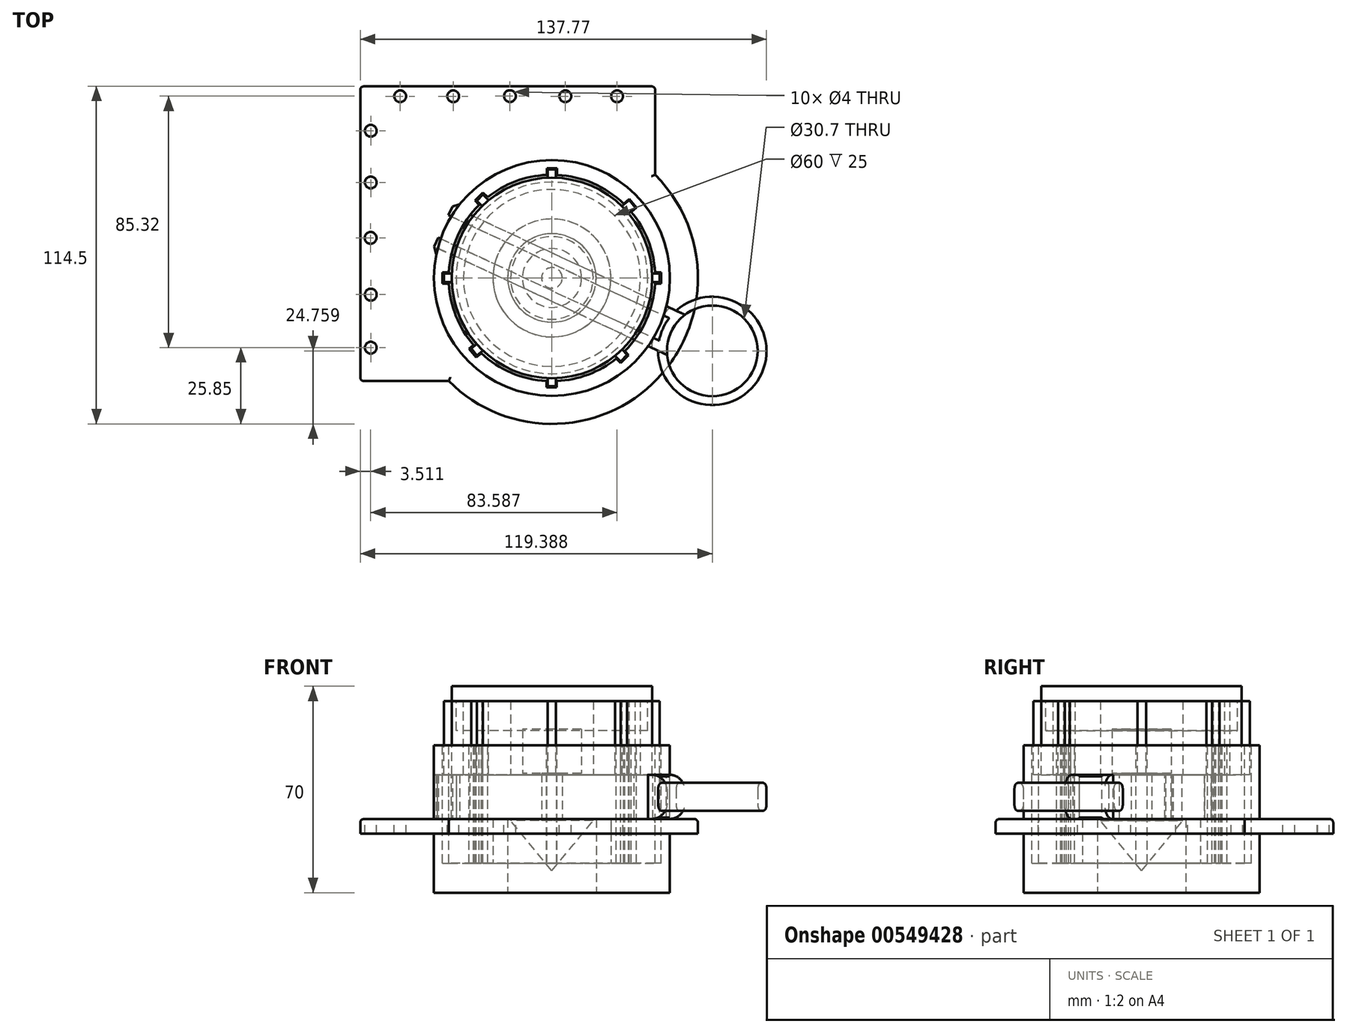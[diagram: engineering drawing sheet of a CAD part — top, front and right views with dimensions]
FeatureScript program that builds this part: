
annotation { "Feature Type Name" : "Feature", "Feature Type Description" : "" }
export const myFeature = defineFeature(function(context is Context, id is Id, definition is map)
    precondition{}
    {
        {
            var Q0;
            Q0=qCreatedBy(makeId("Top.planeOp"),FACE);
            var sketch = newSketch(context, id + "F0", { "sketchPlane" : qUnion([Q0])});
            skCircle(sketch, "E0", {"center": v(0, 0) * mm, "radius": 35 * mm});
            skCircle(sketch, "E1", {"center": v(0, 0) * mm, "radius": 40 * mm});
            skLineSegment(sketch, "E2.bottom", {"start": v(-1.72, 37.22) * mm, "end": v(1.75, 37.22) * mm});
            skLineSegment(sketch, "E2.top", {"start": v(-1.72, 33.39) * mm, "end": v(1.75, 33.39) * mm});
            skLineSegment(sketch, "E2.left", {"start": v(-1.72, 37.22) * mm, "end": v(-1.72, 33.39) * mm});
            skLineSegment(sketch, "E2.right", {"start": v(1.75, 37.22) * mm, "end": v(1.75, 33.39) * mm});
            skLineSegment(sketch, "E3.bottom", {"start": v(-23.4, 28.93) * mm, "end": v(-20.95, 26.48) * mm});
            skLineSegment(sketch, "E3.top", {"start": v(-26.11, 26.22) * mm, "end": v(-23.66, 23.77) * mm});
            skLineSegment(sketch, "E3.left", {"start": v(-23.4, 28.93) * mm, "end": v(-26.11, 26.22) * mm});
            skLineSegment(sketch, "E3.right", {"start": v(-20.95, 26.48) * mm, "end": v(-23.66, 23.77) * mm});
            skLineSegment(sketch, "E4.bottom", {"start": v(-37.15, 1.95) * mm, "end": v(-33.68, 1.95) * mm});
            skLineSegment(sketch, "E4.top", {"start": v(-37.15, -1.88) * mm, "end": v(-33.68, -1.88) * mm});
            skLineSegment(sketch, "E4.left", {"start": v(-37.15, 1.95) * mm, "end": v(-37.15, -1.88) * mm});
            skLineSegment(sketch, "E4.right", {"start": v(-33.68, 1.95) * mm, "end": v(-33.68, -1.88) * mm});
            skLineSegment(sketch, "E5.bottom", {"start": v(1.65, -37.15) * mm, "end": v(-1.82, -37.15) * mm});
            skLineSegment(sketch, "E5.top", {"start": v(1.65, -33.31) * mm, "end": v(-1.82, -33.31) * mm});
            skLineSegment(sketch, "E5.left", {"start": v(1.65, -37.15) * mm, "end": v(1.65, -33.31) * mm});
            skLineSegment(sketch, "E5.right", {"start": v(-1.82, -37.15) * mm, "end": v(-1.82, -33.31) * mm});
            skLineSegment(sketch, "E6.bottom", {"start": v(23.33, -28.86) * mm, "end": v(20.88, -26.41) * mm});
            skLineSegment(sketch, "E6.top", {"start": v(26.04, -26.15) * mm, "end": v(23.6, -23.7) * mm});
            skLineSegment(sketch, "E6.left", {"start": v(23.33, -28.86) * mm, "end": v(26.04, -26.15) * mm});
            skLineSegment(sketch, "E6.right", {"start": v(20.88, -26.41) * mm, "end": v(23.6, -23.7) * mm});
            skLineSegment(sketch, "E7.bottom", {"start": v(37.08, -1.88) * mm, "end": v(33.61, -1.88) * mm});
            skLineSegment(sketch, "E7.top", {"start": v(37.08, 1.95) * mm, "end": v(33.61, 1.95) * mm});
            skLineSegment(sketch, "E7.left", {"start": v(37.08, -1.88) * mm, "end": v(37.08, 1.95) * mm});
            skLineSegment(sketch, "E7.right", {"start": v(33.61, -1.88) * mm, "end": v(33.61, 1.95) * mm});
            skLineSegment(sketch, "E8.bottom", {"start": v(-28.15, -24) * mm, "end": v(-25.5, -21.78) * mm});
            skLineSegment(sketch, "E8.top", {"start": v(-25.68, -26.94) * mm, "end": v(-23.03, -24.71) * mm});
            skLineSegment(sketch, "E8.left", {"start": v(-28.15, -24) * mm, "end": v(-25.68, -26.94) * mm});
            skLineSegment(sketch, "E8.right", {"start": v(-25.5, -21.78) * mm, "end": v(-23.03, -24.71) * mm});
            skLineSegment(sketch, "E9.bottom", {"start": v(23.58, 24.56) * mm, "end": v(26.23, 26.79) * mm});
            skLineSegment(sketch, "E9.top", {"start": v(26.04, 21.62) * mm, "end": v(28.7, 23.85) * mm});
            skLineSegment(sketch, "E9.left", {"start": v(23.58, 24.56) * mm, "end": v(26.04, 21.62) * mm});
            skLineSegment(sketch, "E9.right", {"start": v(26.23, 26.79) * mm, "end": v(28.7, 23.85) * mm});
            skSolve(sketch);
        }
        {
            var Q0;
            Q0 = qSketchRegion(id + "F0", true);
            extrude(context, id + "F1", {"entities" : qUnion([Q0]), "oppositeDirection" : true, "depth" : 50 * mm, "offsetDistance" : 25.4 * mm});
        }
        {
            var Q0;
            Q0=makeQuery(id+"F1.opExtrude","CAP_FACE",FACE,{"disambiguationData":[OSD([sQuery(id+"F0.wireOp",EDGE,"E0"),sQuery(id+"F0.wireOp",EDGE,"E1"),sQuery(id+"F0.wireOp",EDGE,"E2.bottom"),sQuery(id+"F0.wireOp",EDGE,"E2.left"),sQuery(id+"F0.wireOp",EDGE,"E2.right"),sQuery(id+"F0.wireOp",EDGE,"E3.bottom"),sQuery(id+"F0.wireOp",EDGE,"E3.top"),sQuery(id+"F0.wireOp",EDGE,"E3.left"),sQuery(id+"F0.wireOp",EDGE,"E4.bottom"),sQuery(id+"F0.wireOp",EDGE,"E4.top"),sQuery(id+"F0.wireOp",EDGE,"E4.left"),sQuery(id+"F0.wireOp",EDGE,"E5.bottom"),sQuery(id+"F0.wireOp",EDGE,"E5.left"),sQuery(id+"F0.wireOp",EDGE,"E5.right"),sQuery(id+"F0.wireOp",EDGE,"E6.bottom"),sQuery(id+"F0.wireOp",EDGE,"E6.top"),sQuery(id+"F0.wireOp",EDGE,"E6.left"),sQuery(id+"F0.wireOp",EDGE,"E7.bottom"),sQuery(id+"F0.wireOp",EDGE,"E7.top"),sQuery(id+"F0.wireOp",EDGE,"E7.left"),sQuery(id+"F0.wireOp",EDGE,"E8.bottom"),sQuery(id+"F0.wireOp",EDGE,"E8.top"),sQuery(id+"F0.wireOp",EDGE,"E8.left"),sQuery(id+"F0.wireOp",EDGE,"E9.bottom"),sQuery(id+"F0.wireOp",EDGE,"E9.top"),sQuery(id+"F0.wireOp",EDGE,"E9.right")])],"isStart":false});
            var sketch = newSketch(context, id + "F2", { "sketchPlane" : qUnion([Q0])});
            skCircle(sketch, "E10", {"center": v(0, 0) * mm, "radius": 15 * mm});
            skCircle(sketch, "E11", {"center": v(0, 0) * mm, "radius": 40 * mm});
            skSolve(sketch);
        }
        {
            var Q0;
            Q0 = qSketchRegion(id + "F2", true);
            extrude(context, id + "F3", {"entities" : qUnion([Q0]), "operationType" : NewBodyOperationType.ADD, "oppositeDirection" : true, "depth" : 10 * mm, "offsetDistance" : 25.4 * mm});
        }
        {
            var Q0;
            Q0=makeQuery(id+"F3.boolean.opBoolean","MERGE",FACE,{"derivedFrom":[makeQuery(id+"F1.opExtrude","CAP_FACE",FACE,{"disambiguationData":[OSD([sQuery(id+"F0.wireOp",EDGE,"E0"),sQuery(id+"F0.wireOp",EDGE,"E1"),sQuery(id+"F0.wireOp",EDGE,"E2.bottom"),sQuery(id+"F0.wireOp",EDGE,"E2.left"),sQuery(id+"F0.wireOp",EDGE,"E2.right"),sQuery(id+"F0.wireOp",EDGE,"E3.bottom"),sQuery(id+"F0.wireOp",EDGE,"E3.top"),sQuery(id+"F0.wireOp",EDGE,"E3.left"),sQuery(id+"F0.wireOp",EDGE,"E4.bottom"),sQuery(id+"F0.wireOp",EDGE,"E4.top"),sQuery(id+"F0.wireOp",EDGE,"E4.left"),sQuery(id+"F0.wireOp",EDGE,"E5.bottom"),sQuery(id+"F0.wireOp",EDGE,"E5.left"),sQuery(id+"F0.wireOp",EDGE,"E5.right"),sQuery(id+"F0.wireOp",EDGE,"E6.bottom"),sQuery(id+"F0.wireOp",EDGE,"E6.top"),sQuery(id+"F0.wireOp",EDGE,"E6.left"),sQuery(id+"F0.wireOp",EDGE,"E7.bottom"),sQuery(id+"F0.wireOp",EDGE,"E7.top"),sQuery(id+"F0.wireOp",EDGE,"E7.left"),sQuery(id+"F0.wireOp",EDGE,"E8.bottom"),sQuery(id+"F0.wireOp",EDGE,"E8.top"),sQuery(id+"F0.wireOp",EDGE,"E8.left"),sQuery(id+"F0.wireOp",EDGE,"E9.bottom"),sQuery(id+"F0.wireOp",EDGE,"E9.top"),sQuery(id+"F0.wireOp",EDGE,"E9.right")])],"isStart":false}),makeQuery(id+"F3.opExtrude","CAP_FACE",FACE,{"disambiguationData":[OSD([sQuery(id+"F2.wireOp",EDGE,"E10"),sQuery(id+"F2.wireOp",EDGE,"E11")])],"isStart":true})]});
            var sketch = newSketch(context, id + "F4", { "sketchPlane" : qUnion([Q0])});
            skCircle(sketch, "E12", {"center": v(0, 0) * mm, "radius": 15 * mm});
            skCircle(sketch, "E13", {"center": v(0, 0) * mm, "radius": 20 * mm});
            skSolve(sketch);
        }
        {
            var Q0;
            Q0 = qSketchRegion(id + "F4", true);
            extrude(context, id + "F5", {"entities" : qUnion([Q0]), "operationType" : NewBodyOperationType.ADD, "oppositeDirection" : true, "depth" : 25 * mm, "offsetDistance" : 25.4 * mm});
        }
        {
            var Q0;
            Q0=qCreatedBy(makeId("Top.planeOp"),FACE);
            cPlane(context, id + "F6", {"entities" : qUnion([Q0]), "cplaneType" : CPlaneType.OFFSET, "offset" : 25 * mm, "oppositeDirection" : true, "width" : 152.4 * mm, "height" : 152.4 * mm});
        }
        {
            var Q0;
            Q0=qCreatedBy(id+"F6.planeOp",FACE);
            var sketch = newSketch(context, id + "F7", { "sketchPlane" : qUnion([Q0])});
            skLineSegment(sketch, "E14.bottom", {"start": v(-37.23, 25.85) * mm, "end": v(44.34, -12.19) * mm});
            skLineSegment(sketch, "E14.top", {"start": v(-43.56, 12.25) * mm, "end": v(38, -25.78) * mm});
            skLineSegment(sketch, "E14.left", {"start": v(-37.23, 25.85) * mm, "end": v(-43.56, 12.25) * mm});
            skLineSegment(sketch, "E14.right", {"start": v(44.34, -12.19) * mm, "end": v(38, -25.78) * mm});
            skSolve(sketch);
        }
        {
            var Q0;
            Q0 = qSketchRegion(id + "F7", true);
            extrude(context, id + "F8", {"entities" : qUnion([Q0]), "operationType" : NewBodyOperationType.REMOVE, "depth" : 15 * mm, "offsetDistance" : 25.4 * mm});
        }
        {
            var Q0;
            Q0=qCreatedBy(id+"F6.planeOp",FACE);
            var sketch = newSketch(context, id + "F9", { "sketchPlane" : qUnion([Q0])});
            skLineSegment(sketch, "E15.bottom", {"start": v(-33.66, 24.23) * mm, "end": v(43.96, -11.97) * mm});
            skLineSegment(sketch, "E15.top", {"start": v(-35.04, 21.27) * mm, "end": v(42.59, -14.93) * mm});
            skLineSegment(sketch, "E15.left", {"start": v(-33.66, 24.23) * mm, "end": v(-35.04, 21.27) * mm});
            skLineSegment(sketch, "E15.right", {"start": v(43.96, -11.97) * mm, "end": v(42.59, -14.93) * mm});
            skLineSegment(sketch, "E16.bottom", {"start": v(-38.49, 13.66) * mm, "end": v(39.14, -22.54) * mm});
            skLineSegment(sketch, "E16.top", {"start": v(-39.87, 10.7) * mm, "end": v(37.76, -25.5) * mm});
            skLineSegment(sketch, "E16.left", {"start": v(-38.49, 13.66) * mm, "end": v(-39.87, 10.7) * mm});
            skLineSegment(sketch, "E16.right", {"start": v(39.14, -22.54) * mm, "end": v(37.76, -25.5) * mm});
            skLineSegment(sketch, "E17", {"start": v(-33.66, 24.23) * mm, "end": v(-31.36, 24.98) * mm});
            skLineSegment(sketch, "E18", {"start": v(-31.36, 24.98) * mm, "end": v(-32.41, 23.64) * mm});
            skLineSegment(sketch, "E19", {"start": v(-32.41, 23.64) * mm, "end": v(-33.66, 24.23) * mm});
            skLineSegment(sketch, "E20", {"start": v(-39.87, 10.7) * mm, "end": v(-39.25, 8.15) * mm});
            skLineSegment(sketch, "E21", {"start": v(-39.25, 8.15) * mm, "end": v(-38.76, 10.18) * mm});
            skLineSegment(sketch, "E22", {"start": v(-38.76, 10.18) * mm, "end": v(-39.87, 10.7) * mm});
            skCircle(sketch, "E23", {"center": v(54.39, -24.74) * mm, "radius": 18.38 * mm});
            skCircle(sketch, "E24", {"center": v(54.39, -24.74) * mm, "radius": 15.35 * mm});
            skSolve(sketch);
        }
        {
            var Q0;
            Q0 = qSketchRegion(id + "F9", true);
            extrude(context, id + "F10", {"entities" : qUnion([Q0]), "operationType" : NewBodyOperationType.ADD, "depth" : 15 * mm, "offsetDistance" : 25.4 * mm});
        }
        {
            var Q0;
            {var subQ0=sQuery(id+"F9.wireOp",EDGE,"E23");Q0=makeQuery(id+"F10.opExtrude","CAP_EDGE",EDGE,{"disambiguationData":[OSD([subQ0]),TDD([makeQuery(id+"F9.imprint","IMPRINT",EDGE,{"disambiguationData":[TD([[makeQuery(id+"F9.imprint","INTERSECT",VERTEX,{"derivedFrom":[sQuery(id+"F9.wireOp",EDGE,"E15.bottom"),subQ0]}),1.0]])],"derivedFrom":subQ0})])],"isStart":false});}
            fillet(context, id + "F11", {"entities" : qUnion([Q0]), "radius" : 5.08 * mm, "tangentPropagation" : true, "allowEdgeOverflow" : false});
        }
        {
            var Q0;
            {var subQ0=sQuery(id+"F9.wireOp",EDGE,"E23");Q0=makeQuery(id+"F10.opExtrude","CAP_EDGE",EDGE,{"disambiguationData":[OSD([subQ0]),TDD([makeQuery(id+"F9.imprint","IMPRINT",EDGE,{"disambiguationData":[TD([[makeQuery(id+"F9.imprint","INTERSECT",VERTEX,{"derivedFrom":[sQuery(id+"F9.wireOp",EDGE,"E15.bottom"),subQ0]}),1.0]])],"derivedFrom":subQ0})])],"isStart":true});}
            fillet(context, id + "F12", {"entities" : qUnion([Q0]), "radius" : 5.08 * mm, "tangentPropagation" : true, "allowEdgeOverflow" : false});
        }
        {
            var Q0;
            Q0=makeQuery(id+"F10.opExtrude","CAP_EDGE",EDGE,{"disambiguationData":[OSD([sQuery(id+"F9.wireOp",EDGE,"E24")])],"isStart":false});
            fillet(context, id + "F13", {"entities" : qUnion([Q0]), "radius" : 5.33 * mm, "tangentPropagation" : true, "allowEdgeOverflow" : false});
        }
        {
            var Q0;
            Q0=makeQuery(id+"F13.opFillet","BLEND_EDGE",EDGE,{"blendedFrom":[makeQuery(id+"F10.opExtrude","CAP_EDGE",EDGE,{"disambiguationData":[OSD([sQuery(id+"F9.wireOp",EDGE,"E24")])],"isStart":false}),makeQuery(id+"F11.opFillet","BLEND_FACE",FACE,{"disambiguationData":[OSD([sQuery(id+"F9.wireOp",EDGE,"E23")])]})],"blendedInto":[makeQuery(id+"F11.opFillet","BLEND_FACE",FACE,{"disambiguationData":[OSD([sQuery(id+"F9.wireOp",EDGE,"E23")])]})]});
            fillet(context, id + "F14", {"entities" : qUnion([Q0]), "radius" : 1.33 * mm, "tangentPropagation" : true, "allowEdgeOverflow" : false});
        }
        {
            var Q0;
            Q0=makeQuery(id+"F10.opExtrude","CAP_EDGE",EDGE,{"disambiguationData":[OSD([sQuery(id+"F9.wireOp",EDGE,"E24")])],"isStart":true});
            fillet(context, id + "F15", {"entities" : qUnion([Q0]), "radius" : 5.27 * mm, "tangentPropagation" : true, "allowEdgeOverflow" : false});
        }
        {
            var Q0;
            Q0=makeQuery(id+"F15.opFillet","BLEND_EDGE",EDGE,{"blendedFrom":[makeQuery(id+"F10.opExtrude","CAP_EDGE",EDGE,{"disambiguationData":[OSD([sQuery(id+"F9.wireOp",EDGE,"E24")])],"isStart":true}),makeQuery(id+"F12.opFillet","BLEND_FACE",FACE,{"disambiguationData":[OSD([sQuery(id+"F9.wireOp",EDGE,"E23")])]})],"blendedInto":[makeQuery(id+"F12.opFillet","BLEND_FACE",FACE,{"disambiguationData":[OSD([sQuery(id+"F9.wireOp",EDGE,"E23")])]})]});
            fillet(context, id + "F16", {"entities" : qUnion([Q0]), "radius" : 1.35 * mm, "tangentPropagation" : true, "allowEdgeOverflow" : false});
        }
        {
            var Q0;
            Q0=qCreatedBy(makeId("Front.planeOp"),FACE);
            var sketch = newSketch(context, id + "F17", { "sketchPlane" : qUnion([Q0])});
            skLineSegment(sketch, "E25", {"start": v(0, -25.56) * mm, "end": v(-14, -25.56) * mm});
            skLineSegment(sketch, "E26", {"start": v(-14, -25.56) * mm, "end": v(0, -42.53) * mm});
            skLineSegment(sketch, "E27", {"start": v(0, -42.53) * mm, "end": v(0, -25.56) * mm});
            skLineSegment(sketch, "E28", {"start": v(0, 14.89) * mm, "end": v(0, -54.14) * mm, "construction": true});
            skPoint(sketch, "E28.endSnap0", {"position": v(0, -34.05) * mm});
            skSolve(sketch);
        }
        {
            var Q0;
            Q0 = qSketchRegion(id + "F17", true);
            var Q1;
            Q1=sQuery(id+"F17.wireOp",EDGE,"E28");
            revolve(context, id + "F18", {"entities" : qUnion([Q0]), "axis" : qUnion([Q1]), "revolveType" : RevolveType.FULL});
        }
        {
            var Q0;
            Q0=makeQuery(id+"F18.opRevolve","SWEPT_FACE",FACE,{"disambiguationData":[OSD([sQuery(id+"F17.wireOp",EDGE,"E25")])]});
            var sketch = newSketch(context, id + "F19", { "sketchPlane" : qUnion([Q0])});
            skCircle(sketch, "E29", {"center": v(0, 0) * mm, "radius": 3.5 * mm});
            skSolve(sketch);
        }
        {
            var Q0;
            Q0 = qSketchRegion(id + "F19", true);
            extrude(context, id + "F20", {"entities" : qUnion([Q0]), "operationType" : NewBodyOperationType.ADD, "depth" : 16 * mm, "offsetDistance" : 25.4 * mm});
        }
        {
            var Q0;
            Q0=makeQuery(id+"F20.opExtrude","CAP_FACE",FACE,{"disambiguationData":[OSD([sQuery(id+"F19.wireOp",EDGE,"E29")])],"isStart":false});
            var sketch = newSketch(context, id + "F21", { "sketchPlane" : qUnion([Q0])});
            skCircle(sketch, "E30", {"center": v(0, 0) * mm, "radius": 10 * mm});
            skSolve(sketch);
        }
        {
            var Q0;
            Q0 = qSketchRegion(id + "F21", true);
            extrude(context, id + "F22", {"entities" : qUnion([Q0]), "operationType" : NewBodyOperationType.ADD, "depth" : 15 * mm, "offsetDistance" : 25.4 * mm});
        }
        {
            var Q0;
            Q0=makeQuery(id+"F22.opExtrude","CAP_FACE",FACE,{"disambiguationData":[OSD([sQuery(id+"F21.wireOp",EDGE,"E30")])],"isStart":false});
            var sketch = newSketch(context, id + "F23", { "sketchPlane" : qUnion([Q0])});
            skCircle(sketch, "E31", {"center": v(0, 0) * mm, "radius": 10 * mm});
            skSolve(sketch);
        }
        {
            var Q0;
            Q0 = qSketchRegion(id + "F23", true);
            extrude(context, id + "F24", {"entities" : qUnion([Q0]), "operationType" : NewBodyOperationType.ADD, "oppositeDirection" : true, "depth" : 5 * mm, "offsetDistance" : 25.4 * mm});
        }
        {
            var Q0;
            Q0=qCreatedBy(makeId("Top.planeOp"),FACE);
            cPlane(context, id + "F25", {"entities" : qUnion([Q0]), "cplaneType" : CPlaneType.OFFSET, "offset" : 10 * mm, "oppositeDirection" : true, "width" : 152.4 * mm, "height" : 152.4 * mm});
        }
        {
            var Q0;
            Q0=qCreatedBy(id+"F25.planeOp",FACE);
            var sketch = newSketch(context, id + "F26", { "sketchPlane" : qUnion([Q0])});
            skCircle(sketch, "E32", {"center": v(0, 0) * mm, "radius": 14 * mm});
            skSolve(sketch);
        }
        {
            var Q0;
            Q0 = qSketchRegion(id + "F26", true);
            extrude(context, id + "F27", {"entities" : qUnion([Q0]), "depth" : 25 * mm, "offsetDistance" : 25.4 * mm});
        }
        {
            var Q0;
            Q0=makeQuery(id+"F27.opExtrude","CAP_FACE",FACE,{"disambiguationData":[OSD([sQuery(id+"F26.wireOp",EDGE,"E32")])],"isStart":false});
            var sketch = newSketch(context, id + "F28", { "sketchPlane" : qUnion([Q0])});
            skCircle(sketch, "E33", {"center": v(0, 0) * mm, "radius": 34 * mm});
            skLineSegment(sketch, "E34.bottom", {"start": v(-1.39, 36.78) * mm, "end": v(1.37, 36.78) * mm});
            skLineSegment(sketch, "E34.top", {"start": v(-1.39, 33.97) * mm, "end": v(1.37, 33.97) * mm});
            skLineSegment(sketch, "E34.left", {"start": v(-1.39, 36.78) * mm, "end": v(-1.39, 33.97) * mm});
            skLineSegment(sketch, "E34.right", {"start": v(1.37, 36.78) * mm, "end": v(1.37, 33.97) * mm});
            skLineSegment(sketch, "E35.bottom", {"start": v(-1.48, -33.97) * mm, "end": v(1.32, -33.97) * mm});
            skLineSegment(sketch, "E35.top", {"start": v(-1.48, -36.71) * mm, "end": v(1.32, -36.71) * mm});
            skLineSegment(sketch, "E35.left", {"start": v(-1.48, -33.97) * mm, "end": v(-1.48, -36.71) * mm});
            skLineSegment(sketch, "E35.right", {"start": v(1.32, -33.97) * mm, "end": v(1.32, -36.71) * mm});
            skLineSegment(sketch, "E36.bottom", {"start": v(-33.97, 1.5) * mm, "end": v(-36.57, 1.5) * mm});
            skLineSegment(sketch, "E36.top", {"start": v(-33.97, -1.4) * mm, "end": v(-36.57, -1.4) * mm});
            skLineSegment(sketch, "E36.left", {"start": v(-33.97, 1.5) * mm, "end": v(-33.97, -1.4) * mm});
            skLineSegment(sketch, "E36.right", {"start": v(-36.57, 1.5) * mm, "end": v(-36.57, -1.4) * mm});
            skLineSegment(sketch, "E37.bottom", {"start": v(33.97, 1.5) * mm, "end": v(36.54, 1.5) * mm});
            skLineSegment(sketch, "E37.top", {"start": v(33.97, -1.4) * mm, "end": v(36.54, -1.4) * mm});
            skLineSegment(sketch, "E37.left", {"start": v(33.97, 1.5) * mm, "end": v(33.97, -1.4) * mm});
            skLineSegment(sketch, "E37.right", {"start": v(36.54, 1.5) * mm, "end": v(36.54, -1.4) * mm});
            skLineSegment(sketch, "E38.bottom", {"start": v(-21.4, 26.3) * mm, "end": v(-23.5, 24.2) * mm});
            skLineSegment(sketch, "E38.top", {"start": v(-23.36, 28.26) * mm, "end": v(-25.46, 26.16) * mm});
            skLineSegment(sketch, "E38.left", {"start": v(-21.4, 26.3) * mm, "end": v(-23.36, 28.26) * mm});
            skLineSegment(sketch, "E38.right", {"start": v(-23.5, 24.2) * mm, "end": v(-25.46, 26.16) * mm});
            skLineSegment(sketch, "E39.bottom", {"start": v(26.21, 26.42) * mm, "end": v(28.32, 23.9) * mm});
            skLineSegment(sketch, "E39.top", {"start": v(23.65, 24.27) * mm, "end": v(25.76, 21.76) * mm});
            skLineSegment(sketch, "E39.left", {"start": v(26.21, 26.42) * mm, "end": v(23.65, 24.27) * mm});
            skLineSegment(sketch, "E39.right", {"start": v(28.32, 23.9) * mm, "end": v(25.76, 21.76) * mm});
            skLineSegment(sketch, "E40.bottom", {"start": v(-27.31, -23.94) * mm, "end": v(-25.22, -22.2) * mm});
            skLineSegment(sketch, "E40.top", {"start": v(-25.4, -26.25) * mm, "end": v(-23.3, -24.51) * mm});
            skLineSegment(sketch, "E40.left", {"start": v(-27.31, -23.94) * mm, "end": v(-25.4, -26.25) * mm});
            skLineSegment(sketch, "E40.right", {"start": v(-25.22, -22.2) * mm, "end": v(-23.3, -24.51) * mm});
            skLineSegment(sketch, "E41.bottom", {"start": v(23.56, -24.08) * mm, "end": v(25.53, -26.05) * mm});
            skLineSegment(sketch, "E41.top", {"start": v(21.33, -26.3) * mm, "end": v(23.3, -28.27) * mm});
            skLineSegment(sketch, "E41.left", {"start": v(23.56, -24.08) * mm, "end": v(21.33, -26.3) * mm});
            skLineSegment(sketch, "E41.right", {"start": v(25.53, -26.05) * mm, "end": v(23.3, -28.27) * mm});
            skCircle(sketch, "E42", {"center": v(0, 0) * mm, "radius": 14 * mm});
            skCircle(sketch, "E43", {"center": v(0, 0) * mm, "radius": 30 * mm});
            skSolve(sketch);
        }
        {
            var Q0;
            Q0 = qSketchRegion(id + "F28", true);
            extrude(context, id + "F29", {"entities" : qUnion([Q0]), "oppositeDirection" : true, "depth" : 25 * mm, "offsetDistance" : 25.4 * mm});
        }
        {
            var Q0;
            Q0=makeQuery(id+"F29.opExtrude","CAP_FACE",FACE,{"disambiguationData":[OSD([sQuery(id+"F28.wireOp",EDGE,"E33"),sQuery(id+"F28.wireOp",EDGE,"E34.bottom"),sQuery(id+"F28.wireOp",EDGE,"E34.top"),sQuery(id+"F28.wireOp",EDGE,"E34.left"),sQuery(id+"F28.wireOp",EDGE,"E34.right"),sQuery(id+"F28.wireOp",EDGE,"E35.top"),sQuery(id+"F28.wireOp",EDGE,"E35.left"),sQuery(id+"F28.wireOp",EDGE,"E35.right"),sQuery(id+"F28.wireOp",EDGE,"E36.bottom"),sQuery(id+"F28.wireOp",EDGE,"E36.top"),sQuery(id+"F28.wireOp",EDGE,"E36.right"),sQuery(id+"F28.wireOp",EDGE,"E37.bottom"),sQuery(id+"F28.wireOp",EDGE,"E37.top"),sQuery(id+"F28.wireOp",EDGE,"E37.right"),sQuery(id+"F28.wireOp",EDGE,"E38.top"),sQuery(id+"F28.wireOp",EDGE,"E38.left"),sQuery(id+"F28.wireOp",EDGE,"E38.right"),sQuery(id+"F28.wireOp",EDGE,"E39.bottom"),sQuery(id+"F28.wireOp",EDGE,"E39.left"),sQuery(id+"F28.wireOp",EDGE,"E39.right"),sQuery(id+"F28.wireOp",EDGE,"E40.bottom"),sQuery(id+"F28.wireOp",EDGE,"E40.top"),sQuery(id+"F28.wireOp",EDGE,"E40.left"),sQuery(id+"F28.wireOp",EDGE,"E41.bottom"),sQuery(id+"F28.wireOp",EDGE,"E41.top"),sQuery(id+"F28.wireOp",EDGE,"E41.right"),sQuery(id+"F28.wireOp",EDGE,"E43")])],"isStart":true});
            var sketch = newSketch(context, id + "F30", { "sketchPlane" : qUnion([Q0])});
            skCircle(sketch, "E44", {"center": v(0, 0) * mm, "radius": 32.5 * mm});
            skSolve(sketch);
        }
        {
            var Q0;
            Q0 = qSketchRegion(id + "F30", true);
            extrude(context, id + "F31", {"entities" : qUnion([Q0]), "oppositeDirection" : true, "depth" : 10 * mm, "offsetDistance" : 25.4 * mm});
        }
        {
            var Q0;
            Q0=makeQuery(id+"F31.opExtrude","CAP_FACE",FACE,{"disambiguationData":[OSD([sQuery(id+"F30.wireOp",EDGE,"E44")])],"isStart":true});
            var sketch = newSketch(context, id + "F32", { "sketchPlane" : qUnion([Q0])});
            skCircle(sketch, "E45", {"center": v(0, 0) * mm, "radius": 34 * mm});
            skSolve(sketch);
        }
        {
            var Q0;
            Q0 = qSketchRegion(id + "F32", true);
            extrude(context, id + "F33", {"entities" : qUnion([Q0]), "depth" : 5 * mm, "offsetDistance" : 25.4 * mm});
        }
        {
            var Q0;
            Q0=qCreatedBy(makeId("Front.planeOp"),FACE);
            var sketch = newSketch(context, id + "F34", { "sketchPlane" : qUnion([Q0])});
            skArc(sketch, "E46", {"start": v(0, 31.82) * mm, "mid": v(-31.96, 22.35) * mm, "end": v(-40, -10) * mm});
            skLineSegment(sketch, "E47", {"start": v(0, -59.53) * mm, "end": v(0, 76.71) * mm, "construction": true});
            skSolve(sketch);
        }
        {
            var Q0;
            Q0 = qSketchRegion(id + "F34", true);
            var Q1;
            Q1=sQuery(id+"F34.wireOp",EDGE,"E46");
            var Q2;
            Q2=sQuery(id+"F34.wireOp",EDGE,"E47");
            revolve(context, id + "F35", {"bodyType" : ToolBodyType.SURFACE, "entities" : qUnion([Q0]), "surfaceEntities" : qUnion([Q1]), "axis" : qUnion([Q2]), "revolveType" : RevolveType.FULL});
        }
        {
            var Q0;
            Q0=qCreatedBy(id+"F6.planeOp",FACE);
            var sketch = newSketch(context, id + "F36", { "sketchPlane" : qUnion([Q0])});
            skCircle(sketch, "E48", {"center": v(0, 0) * mm, "radius": 40 * mm});
            skArc(sketch, "E49", {"start": v(-35, -35) * mm, "mid": v(35, -35) * mm, "end": v(35, 35) * mm});
            skLineSegment(sketch, "E50", {"start": v(35, 35) * mm, "end": v(35, 65) * mm});
            skLineSegment(sketch, "E51", {"start": v(35, 65) * mm, "end": v(-65, 65) * mm});
            skLineSegment(sketch, "E52", {"start": v(-65, 65) * mm, "end": v(-65, -35) * mm});
            skLineSegment(sketch, "E53", {"start": v(-65, -35) * mm, "end": v(-35, -35) * mm});
            skSolve(sketch);
        }
        {
            var Q0;
            Q0 = qSketchRegion(id + "F36", true);
            extrude(context, id + "F37", {"entities" : qUnion([Q0]), "operationType" : NewBodyOperationType.ADD, "oppositeDirection" : true, "depth" : 5 * mm, "offsetDistance" : 25.4 * mm});
        }
        {
            var Q0;
            Q0=makeQuery(id+"F37.opExtrude","CAP_EDGE",EDGE,{"disambiguationData":[OSD([sQuery(id+"F36.wireOp",EDGE,"E51")])],"isStart":true});
            fillet(context, id + "F38", {"entities" : qUnion([Q0]), "radius" : 1.27 * mm, "tangentPropagation" : true, "allowEdgeOverflow" : false});
        }
        {
            var Q0;
            Q0=makeQuery(id+"F37.opExtrude","CAP_EDGE",EDGE,{"disambiguationData":[OSD([sQuery(id+"F36.wireOp",EDGE,"E52")])],"isStart":true});
            fillet(context, id + "F39", {"entities" : qUnion([Q0]), "radius" : 1.27 * mm, "tangentPropagation" : true, "allowEdgeOverflow" : false});
        }
        {
            var Q0;
            Q0=makeQuery(id+"F37.opExtrude","CAP_EDGE",EDGE,{"disambiguationData":[OSD([sQuery(id+"F36.wireOp",EDGE,"E53")])],"isStart":true});
            fillet(context, id + "F40", {"entities" : qUnion([Q0]), "radius" : 1.27 * mm, "tangentPropagation" : true, "allowEdgeOverflow" : false});
        }
        {
            var Q0;
            Q0=makeQuery(id+"F37.opExtrude","CAP_EDGE",EDGE,{"disambiguationData":[OSD([sQuery(id+"F36.wireOp",EDGE,"E49")])],"isStart":true});
            fillet(context, id + "F41", {"entities" : qUnion([Q0]), "radius" : 1.27 * mm, "tangentPropagation" : true, "allowEdgeOverflow" : false});
        }
        {
            var Q0;
            Q0=makeQuery(id+"F37.opExtrude","CAP_EDGE",EDGE,{"disambiguationData":[OSD([sQuery(id+"F36.wireOp",EDGE,"E50")])],"isStart":true});
            fillet(context, id + "F42", {"entities" : qUnion([Q0]), "radius" : 1.27 * mm, "tangentPropagation" : true, "allowEdgeOverflow" : false});
        }
        {
            var Q0;
            {var subQ0=sQuery(id+"F9.wireOp",EDGE,"E16.top");var subQ2=sQuery(id+"F9.wireOp",EDGE,"E15.top");var subQ5=makeQuery(id+"F10.opExtrude","SWEPT_FACE",FACE,{"disambiguationData":[OSD([subQ2])]});var subQ6=sQuery(id+"F0.wireOp",EDGE,"E0");var subQ7=makeQuery(id+"F1.opExtrude","SWEPT_FACE",FACE,{"disambiguationData":[OSD([subQ6]),TDD([makeQuery(id+"F0.imprint","IMPRINT",EDGE,{"disambiguationData":[TD([[makeQuery(id+"F0.imprint","INTERSECT",VERTEX,{"derivedFrom":[subQ6,sQuery(id+"F0.wireOp",EDGE,"E6.top")]}),-1.0]])],"derivedFrom":subQ6})])]});var subQ9=sQuery(id+"F7.wireOp",EDGE,"E14.top");var subQ11=sQuery(id+"F7.wireOp",EDGE,"E14.bottom");var subQ13=sQuery(id+"F7.wireOp",EDGE,"E14.right");var subQ14=sQuery(id+"F7.wireOp",EDGE,"E14.left");var subQ15=makeQuery(id+"F8.opExtrude","CAP_FACE",FACE,{"disambiguationData":[OSD([subQ11,subQ9,subQ14,subQ13])],"isStart":true});var subQ16=makeQuery(id+"F8.boolean.opBoolean","COPY",FACE,{"disambiguationData":[TD([subQ7])],"derivedFrom":subQ15});var subQ18=makeQuery(id+"F10.opExtrude","SWEPT_FACE",FACE,{"disambiguationData":[OSD([subQ0])]});var subQ19=makeQuery(id+"F1.opExtrude","SWEPT_FACE",FACE,{"disambiguationData":[OSD([subQ6]),TDD([makeQuery(id+"F0.imprint","IMPRINT",EDGE,{"disambiguationData":[TD([[makeQuery(id+"F0.imprint","INTERSECT",VERTEX,{"derivedFrom":[subQ6,sQuery(id+"F0.wireOp",EDGE,"E3.top")]}),-1.0]])],"derivedFrom":subQ6})])]});var subQ20=makeQuery(id+"F8.boolean.opBoolean","COPY",FACE,{"disambiguationData":[TD([subQ19])],"derivedFrom":subQ15});Q0=makeQuery(id+"F37.boolean.opBoolean","MERGE",FACE,{"derivedFrom":[makeQuery(id+"F10.boolean.opBoolean","SPLIT",FACE,{"disambiguationData":[TD([subQ18])],"derivedFrom":subQ20}),makeQuery(id+"F10.boolean.opBoolean","SPLIT",FACE,{"disambiguationData":[TD([subQ5])],"derivedFrom":subQ20}),makeQuery(id+"F10.boolean.opBoolean","SPLIT",FACE,{"disambiguationData":[TD([subQ18])],"derivedFrom":subQ16}),makeQuery(id+"F10.boolean.opBoolean","SPLIT",FACE,{"disambiguationData":[TD([subQ5])],"derivedFrom":subQ16}),makeQuery(id+"F37.opExtrude","CAP_FACE",FACE,{"disambiguationData":[OSD([sQuery(id+"F36.wireOp",EDGE,"E48"),sQuery(id+"F36.wireOp",EDGE,"E49"),sQuery(id+"F36.wireOp",EDGE,"E50"),sQuery(id+"F36.wireOp",EDGE,"E51"),sQuery(id+"F36.wireOp",EDGE,"E52"),sQuery(id+"F36.wireOp",EDGE,"E53")])],"isStart":true})]});}
            var sketch = newSketch(context, id + "F43", { "sketchPlane" : qUnion([Q0])});
            skCircle(sketch, "E54", {"center": v(-14.24, 61.67) * mm, "radius": 2 * mm});
            skCircle(sketch, "E55", {"center": v(22.1, 61.63) * mm, "radius": 2 * mm});
            skCircle(sketch, "E56", {"center": v(4.54, 61.63) * mm, "radius": 2 * mm});
            skCircle(sketch, "E57", {"center": v(-51.48, 61.63) * mm, "radius": 2 * mm});
            skCircle(sketch, "E58", {"center": v(-33.5, 61.63) * mm, "radius": 2 * mm});
            skCircle(sketch, "E59", {"center": v(-61.49, 13.59) * mm, "radius": 2 * mm});
            skCircle(sketch, "E60", {"center": v(-61.44, 49.92) * mm, "radius": 2 * mm});
            skCircle(sketch, "E61", {"center": v(-61.44, 32.37) * mm, "radius": 2 * mm});
            skCircle(sketch, "E62", {"center": v(-61.44, -23.65) * mm, "radius": 2 * mm});
            skCircle(sketch, "E63", {"center": v(-61.44, -5.67) * mm, "radius": 2 * mm});
            skSolve(sketch);
        }
        {
            var Q0;
            Q0 = qSketchRegion(id + "F43", true);
            extrude(context, id + "F44", {"entities" : qUnion([Q0]), "operationType" : NewBodyOperationType.REMOVE, "oppositeDirection" : true, "depth" : 8.38 * mm, "offsetDistance" : 25.4 * mm});
        }
    });
